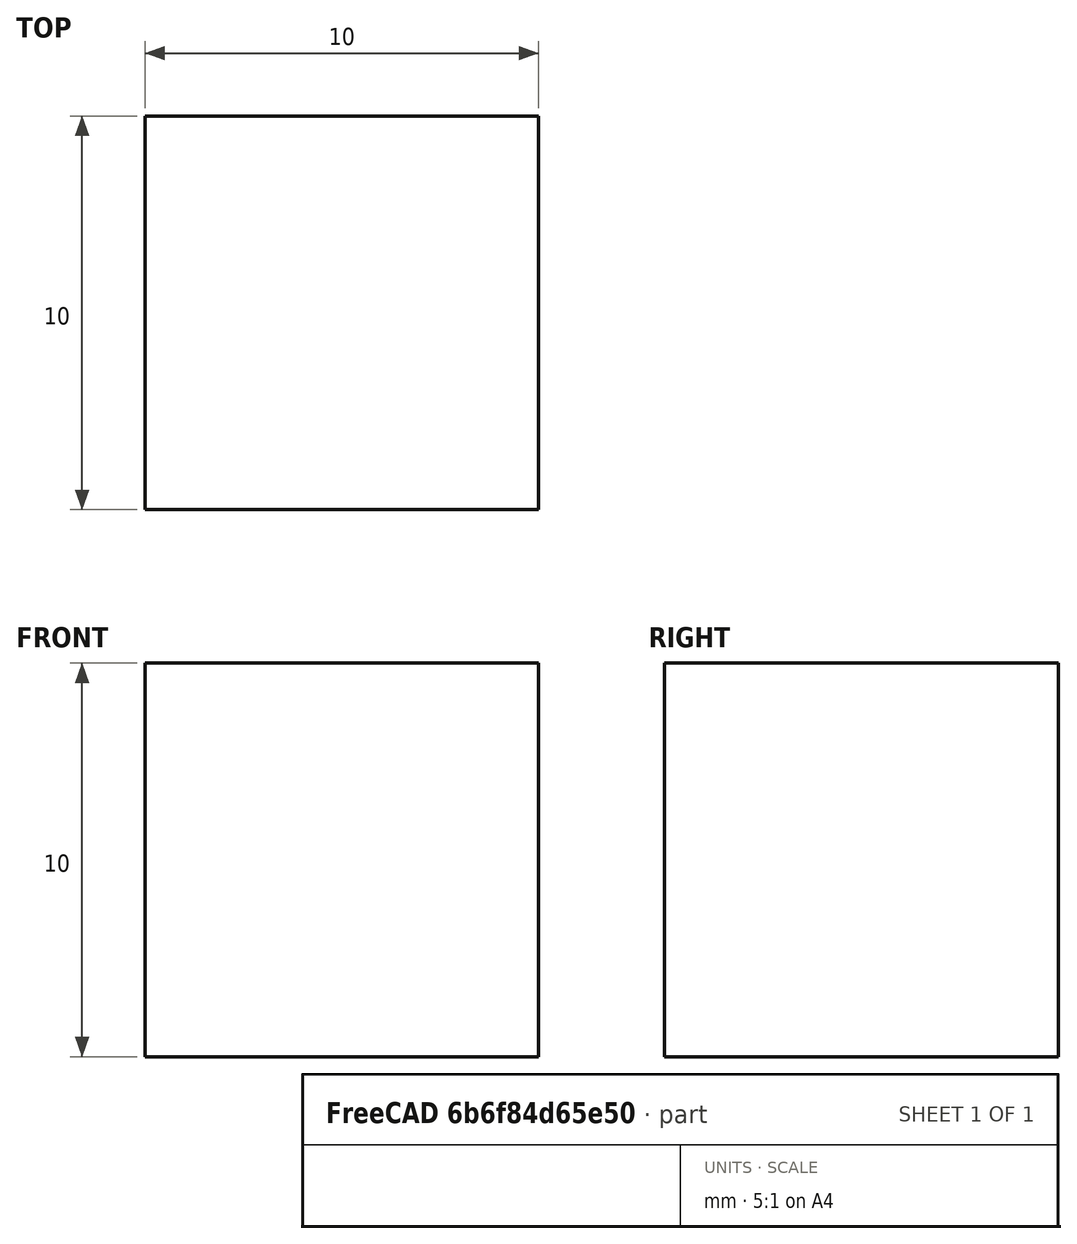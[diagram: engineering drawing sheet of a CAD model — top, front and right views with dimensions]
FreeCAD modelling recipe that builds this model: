
FCSTD DOCUMENT  (FreeCAD 0.17R11495 (Git))
Label: cube_FEM
License: All rights reserved
LicenseURL: http://en.wikipedia.org/wiki/All_rights_reserved
objects: Part::Box×1, Fem::FemMeshObjectPython×1, Fem::FemSolverObjectPython×1, App::MaterialObjectPython×1, Fem::ConstraintFixed×1, Fem::ConstraintPressure×1, Fem::FemResultObjectPython×1, Fem::FemAnalysisPython×1
note: 1 computed .brp shape members not serialized (recipe doc carries the construction recipe); baked Part::Feature solids carry a one-line shape summary decoded from their .brp

FEATURE [Part::Box] Box  label="Cube"
  AttacherType = Attacher::AttachEngine3D
  Height = 10
  Length = 10
  Width = 10
FEATURE [Fem::FemMeshObjectPython] FEMMeshGMSH  # FEM object (typed FeaturePython)
  Algorithm2D = 0
  Algorithm3D = 0
  CharacteristicLengthMax = 0
  CharacteristicLengthMin = 0
  CoherenceMesh = true
  ElementDimension = 0
  ElementOrder = 1
  GeometryTolerance = 1e-06
  HighOrderOptimize = false
  OptimizeNetgen = false
  OptimizeStd = true
  Part = -> Box
  RecombineAll = false
FEATURE [Fem::FemSolverObjectPython] CalculiX  # FEM object (typed FeaturePython)
  AnalysisType = 0
  EigenmodeHighLimit = 1000000
  EigenmodeLowLimit = 0
  EigenmodesCount = 10
  GeometricalNonlinearity = 0
  IterationsControlParameterCutb = 0.25,0.5,0.75,0.85,,,1.5,
  IterationsControlParameterIter = 4,8,9,200,10,400,,200,,
  IterationsControlParameterTimeUse = false
  IterationsThermoMechMaximum = 200
  IterationsUserDefinedIncrementations = false
  IterationsUserDefinedTimeStepLength = false
  MaterialNonlinearity = 0
  MatrixSolverType = 0
  SolverType = FemSolverCalculix
  SplitInputWriter = false
  ThermoMechSteadyState = true
  TimeEnd = 1
  TimeInitialStep = 1
FEATURE [App::MaterialObjectPython] SolidMaterial  # material (typed FeaturePython)
  Category = 0
  Material = Density=1300.0 kg/m^3,+11 more (map truncated)
FEATURE [Fem::ConstraintFixed] FemConstraintFixed
  NormalDirection = (0,0,1)
  Normals = (9) [(0,0,1),(0,0,1),(0,0,1),(0,0,1),(0,0,1),(0,0,1),(0,0,1),(0,0,1),(0,0,1)]
  Points = (9) [(0,0,10),(5,0,10),(10,0,10),(0,5,10),(5,5,10),(10,5,10),(0,10,10),(5,10,10),(10,10,10)]
  References = -> [Box]
FEATURE [Fem::ConstraintPressure] FemConstraintPressure
  NormalDirection = (1,0,0)
  Normals = (9) [(1,0,0),(1,0,0),(1,0,0),(1,0,0),(1,0,0),(1,0,0),(1,0,0),(1,0,0),(1,0,0)]
  Points = (9) [(10,10,0),(10,10,5),(10,10,10),(10,5,0),(10,5,5),(10,5,10),(10,0,0),(10,0,5),(10,0,10)]
  Pressure = 1000
  References = -> [Box]
FEATURE [Fem::FemResultObjectPython] CalculiX_static_results  # FEM object (typed FeaturePython)
  DisplacementLengths = [0,8.4634,0,8.46284,0,10.1239,0,10.1231,7.37645,6.16949,4.83059,3.41288,1.97335,7.92546,6.79074,5.51338,4.12344,2.69923,1.2243,0,0,0,0,0,0,0,0,0,0,0,7.37605,6.17127,4.8276,3.41259,1.97648,7.925,6.7911,5.51254,4.12384,2.6973,1.22675,8.4409,+2032 more]
  DisplacementVectors = (2074) [(0,0,0),(-8.05623,-8.09905e-05,2.5935),(0,0,0),(-8.05549,0.00101779,2.59399),(0,0,0),(-9.48801,-0.528578,-3.49168),(0,0,0),+2067 more]
  Eigenmode = 0
  EigenmodeFrequency = 0
  MaxShear = [2052.74,18.4991,2047.49,18.2407,2739.24,511.044,2724.7,510.976,8.97648,103.059,301.544,544.178,917.652,11.0626,47.2973,200.466,417.127,725.146,1519.12,2024.44,1967.27,1795.36,2055.73,2023.41,2149.7,2178.23,1850.07,1900.68,2086.32,2134.04,+2044 more]
  Mesh = -> FEMMeshGMSH
  NodeNumbers = [1,2,3,4,5,6,7,8,9,10,11,12,13,14,15,16,17,18,19,20,21,22,23,24,25,26,27,28,29,30,31,32,33,34,35,36,37,38,39,40,41,42,43,44,45,46,47,48,49,50,51,52,53,54,55,56,57,58,59,60,61,62,63,64,65,66,67,68,69,+2005 more]
  PrincipalMax = [-1782.02,19.1954,-1780.2,18.8606,7316.31,12.6708,7282.01,12.9332,7.91855,1.30865,11.8665,13.7616,161.995,18.9052,7.52073,14.3089,11.769,22.2167,-114.282,-1836.41,-1988.41,-1799.7,-1973.56,-1832.25,-2212.04,-2172.16,-1926.85,-1997.55,+2046 more]
  PrincipalMed = [-1980.55,11.7567,-1977.36,11.1799,2085.58,-16.0224,2081.48,-16.5009,4.27159,-1.03702,7.87774,2.59087,119.349,3.42748,-5.38616,7.27202,6.90954,-19.9716,-290.703,-2775.91,-2699.73,-2588.42,-2920.93,-2768.65,-3140.46,-3132.29,-2719.39,+2047 more]
  PrincipalMin = [-5887.5,-17.8028,-5875.18,-17.6208,1837.82,-1009.42,1832.61,-1009.02,-10.0344,-204.808,-591.222,-1074.59,-1673.31,-3.22,-87.074,-386.623,-822.485,-1428.08,-3152.52,-5885.29,-5922.94,-5390.42,-6085.02,-5879.08,-6511.45,-6528.63,-5627,+2047 more]
  ResultType = FemResultMechanical
  Stats = [-9.48801,-4.42263,0,-0.622291,-1.78844e-05,0.628077,-3.62549,-0.183614,2.68395,0,4.65385,10.1239,9.11184,1333.18,6411.04,-2212.04,593.173,9644.11,-3140.46,-124.715,4414.06,-6528.63,-873.074,2662.75,4.93553,733.123,3568.74,0,0,0]
  StrainVectors = (2074) [(0.155682,0.107563,-1.00556),(0.00295566,-0.00446755,0.00252336),(0.154224,0.106147,-1.00135),(0.00282425,-0.0043717,0.00250281),+2070 more]
  StressValues = [4009.9,33.8966,4000.05,33.3119,5358.91,1008.05,5329.33,1007.56,16.4358,204.954,601.104,1082.81,1814.36,19.6631,88.8472,397.46,831.835,1429.67,2953.98,3670.44,3631.5,3268.53,3729.15,3669.36,3918.57,3964.57,3374.42,3468.31,3792.27,3888.99,+2044 more]
  StressVectors = (2074) [(-2137.75,-2266.54,-5245.78),(11.3914,-8.47657,10.2344),(-2137.07,-2265.74,-5229.93),(10.8466,-8.41315,9.98628),(2282.06,2713.46,6244.19),+2069 more]
  Time = 0
  UserDefined = [4105.47,36.9982,4094.98,36.4813,5478.49,1022.09,5449.41,1021.95,17.953,206.117,603.088,1088.36,1835.3,22.1252,94.5947,400.932,834.254,1450.29,3038.24,4048.88,3934.53,3590.72,4111.46,4046.83,4299.4,4356.46,3700.14,3801.36,4172.65,4268.08,+2044 more]
FEATURE [Fem::FemAnalysisPython] Analysis  # FEM object (typed FeaturePython)
  Member = -> [CalculiX,FEMMeshGMSH,SolidMaterial,FemConstraintFixed,FemConstraintPressure,CalculiX_static_results]
